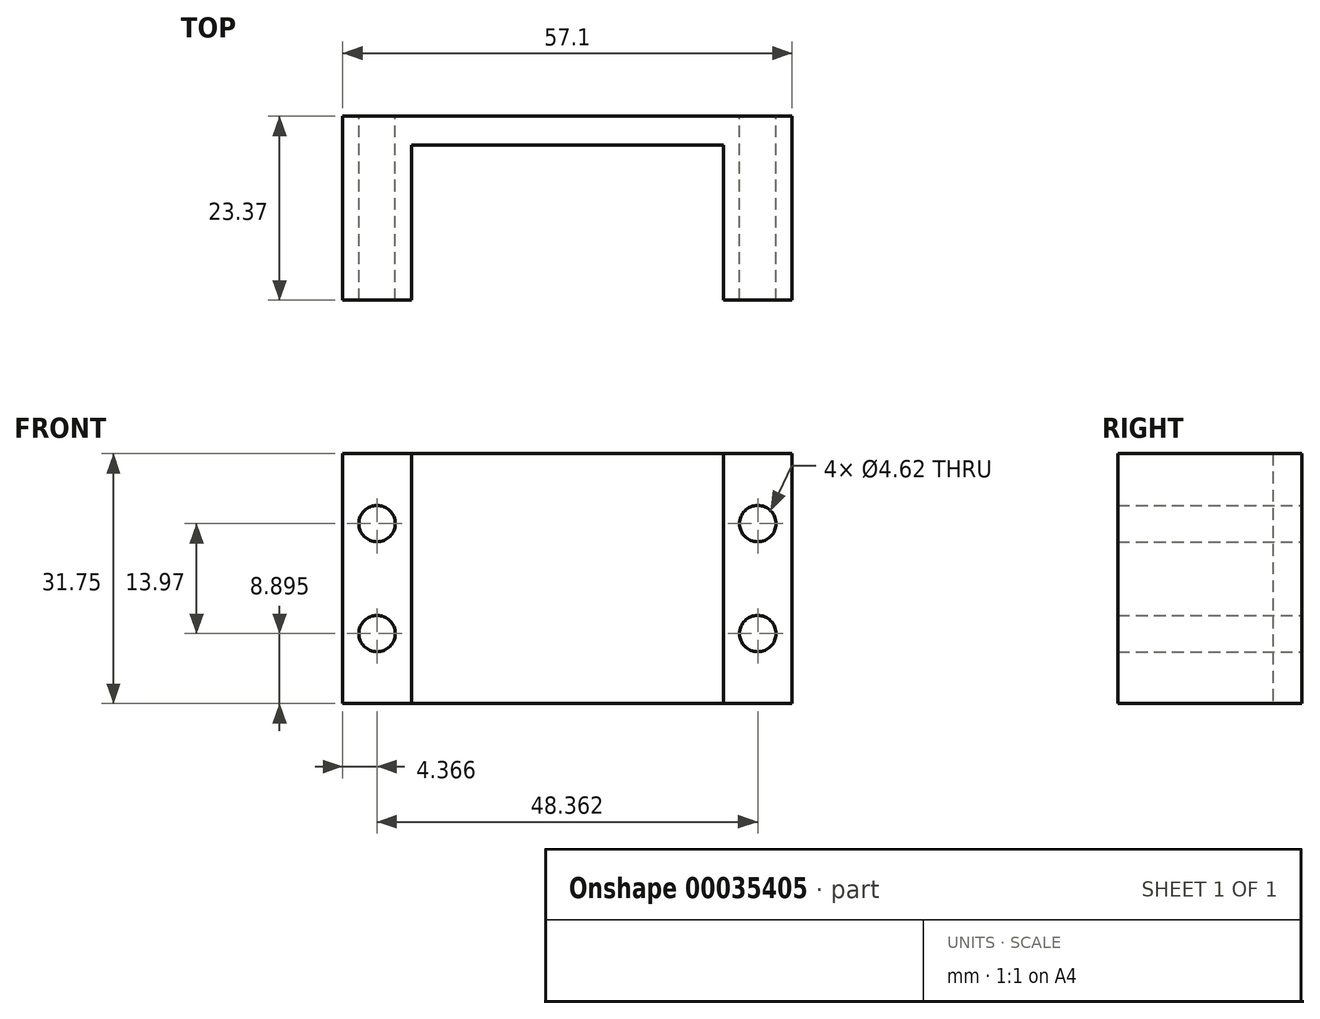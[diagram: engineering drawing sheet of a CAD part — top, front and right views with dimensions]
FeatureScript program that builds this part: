
annotation { "Feature Type Name" : "Feature", "Feature Type Description" : "" }
export const myFeature = defineFeature(function(context is Context, id is Id, definition is map)
    precondition{}
    {
        {
            var Q0;
            Q0=qCreatedBy(makeId("Front.planeOp"),FACE);
            var sketch = newSketch(context, id + "F0", { "sketchPlane" : qUnion([Q0])});
            skLineSegment(sketch, "E0.bottom", {"start": v(-26, 78.3) * mm, "end": v(13.63, 78.3) * mm});
            skLineSegment(sketch, "E0.top", {"start": v(-26, 46.54) * mm, "end": v(13.63, 46.54) * mm});
            skLineSegment(sketch, "E0.left", {"start": v(-26, 78.3) * mm, "end": v(-26, 46.54) * mm});
            skLineSegment(sketch, "E0.right", {"start": v(13.63, 78.3) * mm, "end": v(13.63, 46.54) * mm});
            skCircle(sketch, "E1", {"center": v(18, 55.43) * mm, "radius": 2.31 * mm});
            skCircle(sketch, "E2", {"center": v(18, 69.4) * mm, "radius": 2.31 * mm});
            skCircle(sketch, "E3", {"center": v(-30.36, 69.4) * mm, "radius": 2.31 * mm});
            skCircle(sketch, "E4", {"center": v(-30.36, 55.43) * mm, "radius": 2.31 * mm});
            skLineSegment(sketch, "E5", {"start": v(-26, 78.3) * mm, "end": v(-34.73, 78.3) * mm});
            skLineSegment(sketch, "E6", {"start": v(-34.73, 78.3) * mm, "end": v(-34.73, 46.54) * mm});
            skLineSegment(sketch, "E7", {"start": v(-34.73, 46.54) * mm, "end": v(-26, 46.54) * mm});
            skLineSegment(sketch, "E8", {"start": v(13.63, 78.3) * mm, "end": v(22.37, 78.3) * mm});
            skLineSegment(sketch, "E9", {"start": v(22.37, 78.3) * mm, "end": v(22.37, 46.54) * mm});
            skLineSegment(sketch, "E10", {"start": v(22.37, 46.54) * mm, "end": v(13.63, 46.54) * mm});
            skSolve(sketch);
        }
        {
            var Q0;
            Q0=makeQuery(id+"F0.imprint","IMPRINT",FACE,{"disambiguationData":[TD([[makeQuery(id+"F0.imprint","IMPRINT",EDGE,{"derivedFrom":sQuery(id+"F0.wireOp",EDGE,"E0.left")}),-1.0]])]});
            var Q1;
            Q1=makeQuery(id+"F0.imprint","IMPRINT",FACE,{"disambiguationData":[TD([[makeQuery(id+"F0.imprint","IMPRINT",EDGE,{"derivedFrom":sQuery(id+"F0.wireOp",EDGE,"E0.right")}),1.0]])]});
            extrude(context, id + "F1", {"entities" : qUnion([Q0, Q1]), "depth" : 23.37 * mm});
        }
        {
            var Q0;
            Q0=makeQuery(id+"F0.imprint","IMPRINT",FACE,{"disambiguationData":[TD([[makeQuery(id+"F0.imprint","IMPRINT",EDGE,{"derivedFrom":sQuery(id+"F0.wireOp",EDGE,"E0.bottom")}),-1.0]])]});
            extrude(context, id + "F2", {"entities" : qUnion([Q0]), "operationType" : NewBodyOperationType.ADD, "depth" : 3.68 * mm});
        }
    });
